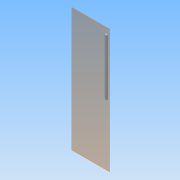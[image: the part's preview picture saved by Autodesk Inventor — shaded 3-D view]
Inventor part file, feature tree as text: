
AUTODESK INVENTOR PART (.ipt)
format: ipt  version: 2013 (Build 170138000, 138)  size: 78,848 bytes
history: native  units: in
note: dims shown in document units (in); Inventor stores cm internally (conversion verified against a paired STEP export)
features: extrude x2, sketch x2, plane x1
ambient origin geometry x8: Origin, YZ Plane, XZ Plane, XY Plane, X Axis, Y Axis, Z Axis, Center Point
bodies: Solid1 (feature_tree)
feature tree (5):
  plane  "Work Plane1"
  extrude  "Extrusion1"  Depth=1.5in
  extrude  "Extrusion3"  TaperAngle=0.0deg  [1 undecoded]
  sketch  "Sketch1"  dims[d0=39.0in d2=1.5in]
  sketch  "Sketch3"  dims[d3=1.0in d4=0.0in d10=0.5in d11=38.5in d12=0.3332in d13=0.0in]
note: 1 required parameter value undecoded (feature->parameter linkage not recoverable at this tier; creation-order binding heuristic only, values carry confidence <= 0.55)
